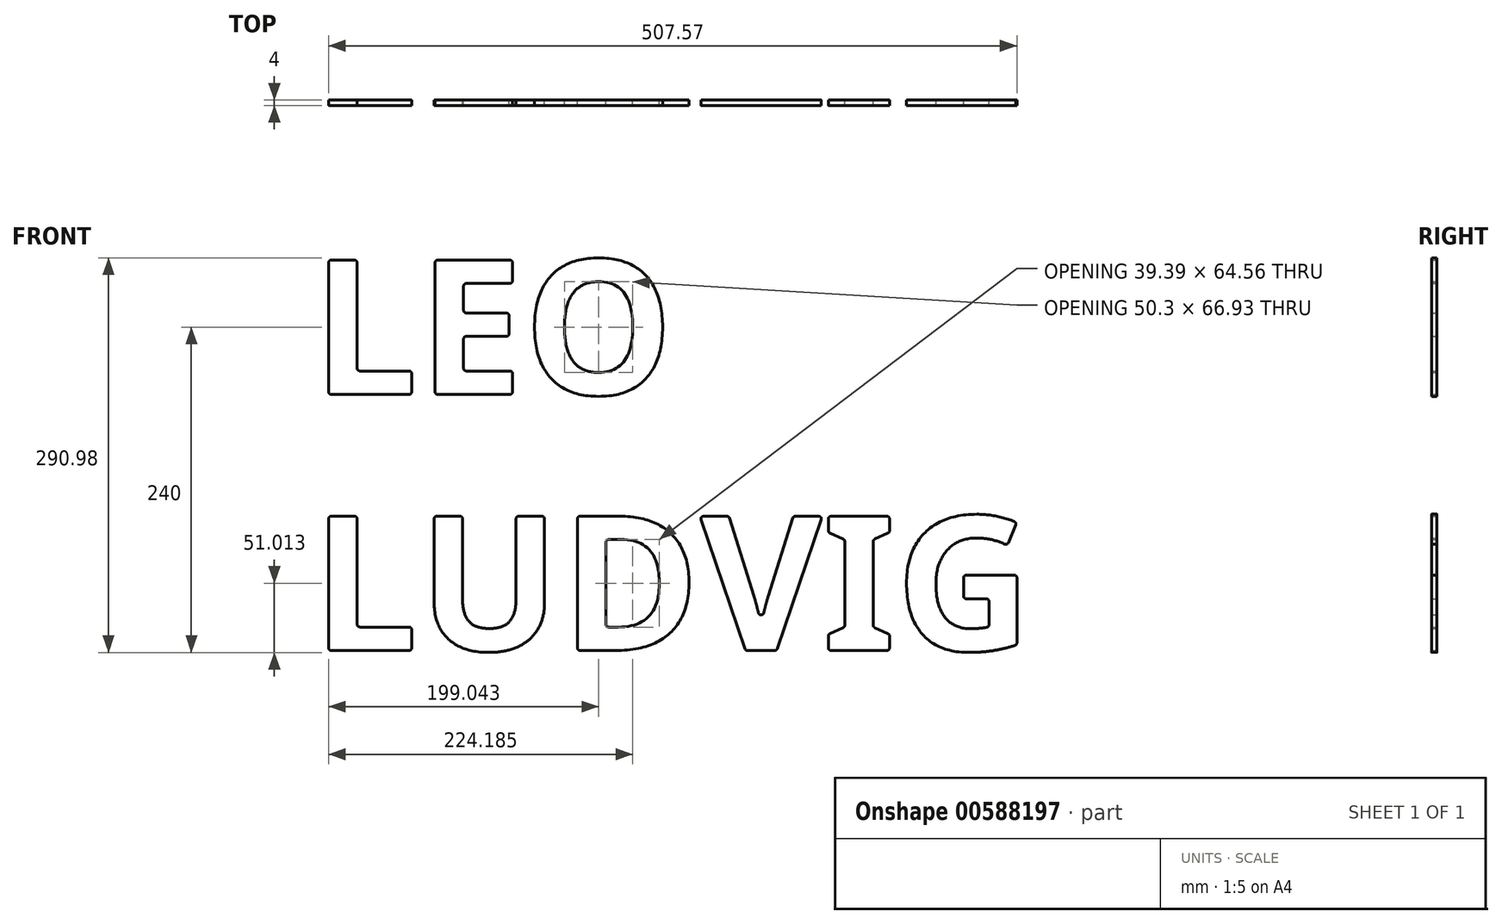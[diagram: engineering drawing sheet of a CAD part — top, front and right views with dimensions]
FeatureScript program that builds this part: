
annotation { "Feature Type Name" : "Feature", "Feature Type Description" : "" }
export const myFeature = defineFeature(function(context is Context, id is Id, definition is map)
    precondition{}
    {
        {
            var Q0;
            Q0=qCreatedBy(makeId("Front.planeOp"),FACE);
            var sketch = newSketch(context, id + "F0", { "sketchPlane" : qUnion([Q0])});
            skText(sketch, "E0", { "text": "LEO\nLUDVIG\n", "fontName": "NotoSans-Bold.ttf"});
            const initialGuessF0  = {"E0": [-0.26453, 0, 1, 0, 0.1]};
            skSetInitialGuess(sketch, initialGuessF0);
            skSolve(sketch);
        }
        {
            var Q0;
            Q0 = qSketchRegion(id + "F0", true);
            extrude(context, id + "F1", {"entities" : qUnion([Q0]), "depth" : 4 * mm, "offsetDistance" : 25 * mm});
        }
        {
            var Q0;
            Q0=makeQuery(id+"F1.opExtrude","SWEPT_EDGE",EDGE,{"disambiguationData":[OSD([sQuery(id+"F0.wireOp",EDGE,"E0.sketch_text.stroke-0"),sQuery(id+"F0.wireOp",EDGE,"E0.sketch_text.stroke-1")])]});
            var Q1;
            Q1=makeQuery(id+"F1.opExtrude","SWEPT_EDGE",EDGE,{"disambiguationData":[OSD([sQuery(id+"F0.wireOp",EDGE,"E0.sketch_text.stroke-1"),sQuery(id+"F0.wireOp",EDGE,"E0.sketch_text.stroke-2")])]});
            var Q2;
            Q2=makeQuery(id+"F1.opExtrude","SWEPT_EDGE",EDGE,{"disambiguationData":[OSD([sQuery(id+"F0.wireOp",EDGE,"E0.sketch_text.stroke-0"),sQuery(id+"F0.wireOp",EDGE,"E0.sketch_text.stroke-5")])]});
            var Q3;
            Q3=makeQuery(id+"F1.opExtrude","SWEPT_EDGE",EDGE,{"disambiguationData":[OSD([sQuery(id+"F0.wireOp",EDGE,"E0.sketch_text.stroke-3"),sQuery(id+"F0.wireOp",EDGE,"E0.sketch_text.stroke-4")])]});
            var Q4;
            Q4=makeQuery(id+"F1.opExtrude","SWEPT_EDGE",EDGE,{"disambiguationData":[OSD([sQuery(id+"F0.wireOp",EDGE,"E0.sketch_text.stroke-2"),sQuery(id+"F0.wireOp",EDGE,"E0.sketch_text.stroke-3")])]});
            var Q5;
            Q5=makeQuery(id+"F1.opExtrude","SWEPT_EDGE",EDGE,{"disambiguationData":[OSD([sQuery(id+"F0.wireOp",EDGE,"E0.sketch_text.stroke-4"),sQuery(id+"F0.wireOp",EDGE,"E0.sketch_text.stroke-5")])]});
            var Q6;
            Q6=makeQuery(id+"F1.opExtrude","SWEPT_EDGE",EDGE,{"disambiguationData":[OSD([sQuery(id+"F0.wireOp",EDGE,"E0.sketch_text.stroke-15"),sQuery(id+"F0.wireOp",EDGE,"E0.sketch_text.stroke-16")])]});
            var Q7;
            Q7=makeQuery(id+"F1.opExtrude","SWEPT_EDGE",EDGE,{"disambiguationData":[OSD([sQuery(id+"F0.wireOp",EDGE,"E0.sketch_text.stroke-16"),sQuery(id+"F0.wireOp",EDGE,"E0.sketch_text.stroke-17")])]});
            var Q8;
            Q8=makeQuery(id+"F1.opExtrude","SWEPT_EDGE",EDGE,{"disambiguationData":[OSD([sQuery(id+"F0.wireOp",EDGE,"E0.sketch_text.stroke-6"),sQuery(id+"F0.wireOp",EDGE,"E0.sketch_text.stroke-17")])]});
            var Q9;
            Q9=makeQuery(id+"F1.opExtrude","SWEPT_EDGE",EDGE,{"disambiguationData":[OSD([sQuery(id+"F0.wireOp",EDGE,"E0.sketch_text.stroke-13"),sQuery(id+"F0.wireOp",EDGE,"E0.sketch_text.stroke-14")])]});
            var Q10;
            Q10=makeQuery(id+"F1.opExtrude","SWEPT_EDGE",EDGE,{"disambiguationData":[OSD([sQuery(id+"F0.wireOp",EDGE,"E0.sketch_text.stroke-12"),sQuery(id+"F0.wireOp",EDGE,"E0.sketch_text.stroke-13")])]});
            var Q11;
            Q11=makeQuery(id+"F1.opExtrude","SWEPT_EDGE",EDGE,{"disambiguationData":[OSD([sQuery(id+"F0.wireOp",EDGE,"E0.sketch_text.stroke-11"),sQuery(id+"F0.wireOp",EDGE,"E0.sketch_text.stroke-12")])]});
            var Q12;
            Q12=makeQuery(id+"F1.opExtrude","SWEPT_EDGE",EDGE,{"disambiguationData":[OSD([sQuery(id+"F0.wireOp",EDGE,"E0.sketch_text.stroke-9"),sQuery(id+"F0.wireOp",EDGE,"E0.sketch_text.stroke-10")])]});
            var Q13;
            Q13=makeQuery(id+"F1.opExtrude","SWEPT_EDGE",EDGE,{"disambiguationData":[OSD([sQuery(id+"F0.wireOp",EDGE,"E0.sketch_text.stroke-8"),sQuery(id+"F0.wireOp",EDGE,"E0.sketch_text.stroke-9")])]});
            var Q14;
            Q14=makeQuery(id+"F1.opExtrude","SWEPT_EDGE",EDGE,{"disambiguationData":[OSD([sQuery(id+"F0.wireOp",EDGE,"E0.sketch_text.stroke-7"),sQuery(id+"F0.wireOp",EDGE,"E0.sketch_text.stroke-8")])]});
            var Q15;
            Q15=makeQuery(id+"F1.opExtrude","SWEPT_EDGE",EDGE,{"disambiguationData":[OSD([sQuery(id+"F0.wireOp",EDGE,"E0.sketch_text.stroke-6"),sQuery(id+"F0.wireOp",EDGE,"E0.sketch_text.stroke-7")])]});
            var Q16;
            Q16=makeQuery(id+"F1.opExtrude","SWEPT_EDGE",EDGE,{"disambiguationData":[OSD([sQuery(id+"F0.wireOp",EDGE,"E0.sketch_text.stroke-14"),sQuery(id+"F0.wireOp",EDGE,"E0.sketch_text.stroke-15")])]});
            var Q17;
            Q17=makeQuery(id+"F1.opExtrude","SWEPT_EDGE",EDGE,{"disambiguationData":[OSD([sQuery(id+"F0.wireOp",EDGE,"E0.sketch_text.stroke-10"),sQuery(id+"F0.wireOp",EDGE,"E0.sketch_text.stroke-11")])]});
            var Q18;
            Q18=makeQuery(id+"F1.opExtrude","SWEPT_EDGE",EDGE,{"disambiguationData":[OSD([sQuery(id+"F0.wireOp",EDGE,"E0.sketch_text.stroke-44"),sQuery(id+"F0.wireOp",EDGE,"E0.sketch_text.stroke-45")])]});
            var Q19;
            Q19=makeQuery(id+"F1.opExtrude","SWEPT_EDGE",EDGE,{"disambiguationData":[OSD([sQuery(id+"F0.wireOp",EDGE,"E0.sketch_text.stroke-45"),sQuery(id+"F0.wireOp",EDGE,"E0.sketch_text.stroke-46")])]});
            var Q20;
            Q20=makeQuery(id+"F1.opExtrude","SWEPT_EDGE",EDGE,{"disambiguationData":[OSD([sQuery(id+"F0.wireOp",EDGE,"E0.sketch_text.stroke-51"),sQuery(id+"F0.wireOp",EDGE,"E0.sketch_text.stroke-52")])]});
            var Q21;
            Q21=makeQuery(id+"F1.opExtrude","SWEPT_EDGE",EDGE,{"disambiguationData":[OSD([sQuery(id+"F0.wireOp",EDGE,"E0.sketch_text.stroke-38"),sQuery(id+"F0.wireOp",EDGE,"E0.sketch_text.stroke-52")])]});
            var Q22;
            Q22=makeQuery(id+"F1.opExtrude","SWEPT_EDGE",EDGE,{"disambiguationData":[OSD([sQuery(id+"F0.wireOp",EDGE,"E0.sketch_text.stroke-56"),sQuery(id+"F0.wireOp",EDGE,"E0.sketch_text.stroke-57")])]});
            var Q23;
            Q23=makeQuery(id+"F1.opExtrude","SWEPT_EDGE",EDGE,{"disambiguationData":[OSD([sQuery(id+"F0.wireOp",EDGE,"E0.sketch_text.stroke-62"),sQuery(id+"F0.wireOp",EDGE,"E0.sketch_text.stroke-63")])]});
            var Q24;
            Q24=makeQuery(id+"F1.opExtrude","SWEPT_EDGE",EDGE,{"disambiguationData":[OSD([sQuery(id+"F0.wireOp",EDGE,"E0.sketch_text.stroke-61"),sQuery(id+"F0.wireOp",EDGE,"E0.sketch_text.stroke-62")])]});
            var Q25;
            Q25=makeQuery(id+"F1.opExtrude","SWEPT_EDGE",EDGE,{"disambiguationData":[OSD([sQuery(id+"F0.wireOp",EDGE,"E0.sketch_text.stroke-55"),sQuery(id+"F0.wireOp",EDGE,"E0.sketch_text.stroke-56")])]});
            var Q26;
            Q26=makeQuery(id+"F1.opExtrude","SWEPT_EDGE",EDGE,{"disambiguationData":[OSD([sQuery(id+"F0.wireOp",EDGE,"E0.sketch_text.stroke-67"),sQuery(id+"F0.wireOp",EDGE,"E0.sketch_text.stroke-68")])]});
            var Q27;
            Q27=makeQuery(id+"F1.opExtrude","SWEPT_EDGE",EDGE,{"disambiguationData":[OSD([sQuery(id+"F0.wireOp",EDGE,"E0.sketch_text.stroke-66"),sQuery(id+"F0.wireOp",EDGE,"E0.sketch_text.stroke-67")])]});
            var Q28;
            Q28=makeQuery(id+"F1.opExtrude","SWEPT_EDGE",EDGE,{"disambiguationData":[OSD([sQuery(id+"F0.wireOp",EDGE,"E0.sketch_text.stroke-72"),sQuery(id+"F0.wireOp",EDGE,"E0.sketch_text.stroke-73")])]});
            var Q29;
            Q29=makeQuery(id+"F1.opExtrude","SWEPT_EDGE",EDGE,{"disambiguationData":[OSD([sQuery(id+"F0.wireOp",EDGE,"E0.sketch_text.stroke-73"),sQuery(id+"F0.wireOp",EDGE,"E0.sketch_text.stroke-74")])]});
            var Q30;
            Q30=makeQuery(id+"F1.opExtrude","SWEPT_EDGE",EDGE,{"disambiguationData":[OSD([sQuery(id+"F0.wireOp",EDGE,"E0.sketch_text.stroke-70"),sQuery(id+"F0.wireOp",EDGE,"E0.sketch_text.stroke-71")])]});
            var Q31;
            Q31=makeQuery(id+"F1.opExtrude","SWEPT_EDGE",EDGE,{"disambiguationData":[OSD([sQuery(id+"F0.wireOp",EDGE,"E0.sketch_text.stroke-68"),sQuery(id+"F0.wireOp",EDGE,"E0.sketch_text.stroke-69")])]});
            var Q32;
            Q32=makeQuery(id+"F1.opExtrude","SWEPT_EDGE",EDGE,{"disambiguationData":[OSD([sQuery(id+"F0.wireOp",EDGE,"E0.sketch_text.stroke-69"),sQuery(id+"F0.wireOp",EDGE,"E0.sketch_text.stroke-70")])]});
            var Q33;
            Q33=makeQuery(id+"F1.opExtrude","SWEPT_EDGE",EDGE,{"disambiguationData":[OSD([sQuery(id+"F0.wireOp",EDGE,"E0.sketch_text.stroke-65"),sQuery(id+"F0.wireOp",EDGE,"E0.sketch_text.stroke-74")])]});
            var Q34;
            Q34=makeQuery(id+"F1.opExtrude","SWEPT_EDGE",EDGE,{"disambiguationData":[OSD([sQuery(id+"F0.wireOp",EDGE,"E0.sketch_text.stroke-65"),sQuery(id+"F0.wireOp",EDGE,"E0.sketch_text.stroke-66")])]});
            var Q35;
            Q35=makeQuery(id+"F1.opExtrude","SWEPT_EDGE",EDGE,{"disambiguationData":[OSD([sQuery(id+"F0.wireOp",EDGE,"E0.sketch_text.stroke-80"),sQuery(id+"F0.wireOp",EDGE,"E0.sketch_text.stroke-81")])]});
            var Q36;
            Q36=makeQuery(id+"F1.opExtrude","SWEPT_EDGE",EDGE,{"disambiguationData":[OSD([sQuery(id+"F0.wireOp",EDGE,"E0.sketch_text.stroke-81"),sQuery(id+"F0.wireOp",EDGE,"E0.sketch_text.stroke-82")])]});
            var Q37;
            Q37=makeQuery(id+"F1.opExtrude","SWEPT_EDGE",EDGE,{"disambiguationData":[OSD([sQuery(id+"F0.wireOp",EDGE,"E0.sketch_text.stroke-79"),sQuery(id+"F0.wireOp",EDGE,"E0.sketch_text.stroke-80")])]});
            var Q38;
            Q38=makeQuery(id+"F1.opExtrude","SWEPT_EDGE",EDGE,{"disambiguationData":[OSD([sQuery(id+"F0.wireOp",EDGE,"E0.sketch_text.stroke-78"),sQuery(id+"F0.wireOp",EDGE,"E0.sketch_text.stroke-79")])]});
            var Q39;
            Q39=makeQuery(id+"F1.opExtrude","SWEPT_EDGE",EDGE,{"disambiguationData":[OSD([sQuery(id+"F0.wireOp",EDGE,"E0.sketch_text.stroke-75"),sQuery(id+"F0.wireOp",EDGE,"E0.sketch_text.stroke-76")])]});
            var Q40;
            Q40=makeQuery(id+"F1.opExtrude","SWEPT_EDGE",EDGE,{"disambiguationData":[OSD([sQuery(id+"F0.wireOp",EDGE,"E0.sketch_text.stroke-76"),sQuery(id+"F0.wireOp",EDGE,"E0.sketch_text.stroke-77")])]});
            var Q41;
            Q41=makeQuery(id+"F1.opExtrude","SWEPT_EDGE",EDGE,{"disambiguationData":[OSD([sQuery(id+"F0.wireOp",EDGE,"E0.sketch_text.stroke-77"),sQuery(id+"F0.wireOp",EDGE,"E0.sketch_text.stroke-78")])]});
            var Q42;
            Q42=makeQuery(id+"F1.opExtrude","SWEPT_EDGE",EDGE,{"disambiguationData":[OSD([sQuery(id+"F0.wireOp",EDGE,"E0.sketch_text.stroke-75"),sQuery(id+"F0.wireOp",EDGE,"E0.sketch_text.stroke-86")])]});
            var Q43;
            Q43=makeQuery(id+"F1.opExtrude","SWEPT_EDGE",EDGE,{"disambiguationData":[OSD([sQuery(id+"F0.wireOp",EDGE,"E0.sketch_text.stroke-84"),sQuery(id+"F0.wireOp",EDGE,"E0.sketch_text.stroke-85")])]});
            var Q44;
            Q44=makeQuery(id+"F1.opExtrude","SWEPT_EDGE",EDGE,{"disambiguationData":[OSD([sQuery(id+"F0.wireOp",EDGE,"E0.sketch_text.stroke-85"),sQuery(id+"F0.wireOp",EDGE,"E0.sketch_text.stroke-86")])]});
            var Q45;
            Q45=makeQuery(id+"F1.opExtrude","SWEPT_EDGE",EDGE,{"disambiguationData":[OSD([sQuery(id+"F0.wireOp",EDGE,"E0.sketch_text.stroke-82"),sQuery(id+"F0.wireOp",EDGE,"E0.sketch_text.stroke-83")])]});
            var Q46;
            Q46=makeQuery(id+"F1.opExtrude","SWEPT_EDGE",EDGE,{"disambiguationData":[OSD([sQuery(id+"F0.wireOp",EDGE,"E0.sketch_text.stroke-83"),sQuery(id+"F0.wireOp",EDGE,"E0.sketch_text.stroke-84")])]});
            var Q47;
            Q47=makeQuery(id+"F1.opExtrude","SWEPT_EDGE",EDGE,{"disambiguationData":[OSD([sQuery(id+"F0.wireOp",EDGE,"E0.sketch_text.stroke-95"),sQuery(id+"F0.wireOp",EDGE,"E0.sketch_text.stroke-96")])]});
            var Q48;
            Q48=makeQuery(id+"F1.opExtrude","SWEPT_EDGE",EDGE,{"disambiguationData":[OSD([sQuery(id+"F0.wireOp",EDGE,"E0.sketch_text.stroke-96"),sQuery(id+"F0.wireOp",EDGE,"E0.sketch_text.stroke-97")])]});
            var Q49;
            Q49=makeQuery(id+"F1.opExtrude","SWEPT_EDGE",EDGE,{"disambiguationData":[OSD([sQuery(id+"F0.wireOp",EDGE,"E0.sketch_text.stroke-87"),sQuery(id+"F0.wireOp",EDGE,"E0.sketch_text.stroke-88")])]});
            var Q50;
            Q50=makeQuery(id+"F1.opExtrude","SWEPT_EDGE",EDGE,{"disambiguationData":[OSD([sQuery(id+"F0.wireOp",EDGE,"E0.sketch_text.stroke-102"),sQuery(id+"F0.wireOp",EDGE,"E0.sketch_text.stroke-103")])]});
            var Q51;
            Q51=makeQuery(id+"F1.opExtrude","SWEPT_EDGE",EDGE,{"disambiguationData":[OSD([sQuery(id+"F0.wireOp",EDGE,"E0.sketch_text.stroke-87"),sQuery(id+"F0.wireOp",EDGE,"E0.sketch_text.stroke-105")])]});
            var Q52;
            Q52=makeQuery(id+"F1.opExtrude","SWEPT_EDGE",EDGE,{"disambiguationData":[OSD([sQuery(id+"F0.wireOp",EDGE,"E0.sketch_text.stroke-104"),sQuery(id+"F0.wireOp",EDGE,"E0.sketch_text.stroke-105")])]});
            var Q53;
            Q53=makeQuery(id+"F1.opExtrude","SWEPT_EDGE",EDGE,{"disambiguationData":[OSD([sQuery(id+"F0.wireOp",EDGE,"E0.sketch_text.stroke-103"),sQuery(id+"F0.wireOp",EDGE,"E0.sketch_text.stroke-104")])]});
            var Q54;
            Q54=makeQuery(id+"F1.opExtrude","SWEPT_EDGE",EDGE,{"disambiguationData":[OSD([sQuery(id+"F0.wireOp",EDGE,"E0.sketch_text.stroke-88"),sQuery(id+"F0.wireOp",EDGE,"E0.sketch_text.stroke-89")])]});
            var Q55;
            Q55=makeQuery(id+"F1.opExtrude","SWEPT_EDGE",EDGE,{"disambiguationData":[OSD([sQuery(id+"F0.wireOp",EDGE,"E0.sketch_text.stroke-32"),sQuery(id+"F0.wireOp",EDGE,"E0.sketch_text.stroke-33")])]});
            var Q56;
            Q56=makeQuery(id+"F1.opExtrude","SWEPT_EDGE",EDGE,{"disambiguationData":[OSD([sQuery(id+"F0.wireOp",EDGE,"E0.sketch_text.stroke-33"),sQuery(id+"F0.wireOp",EDGE,"E0.sketch_text.stroke-34")])]});
            var Q57;
            Q57=makeQuery(id+"F1.opExtrude","SWEPT_EDGE",EDGE,{"disambiguationData":[OSD([sQuery(id+"F0.wireOp",EDGE,"E0.sketch_text.stroke-35"),sQuery(id+"F0.wireOp",EDGE,"E0.sketch_text.stroke-36")])]});
            var Q58;
            Q58=makeQuery(id+"F1.opExtrude","SWEPT_EDGE",EDGE,{"disambiguationData":[OSD([sQuery(id+"F0.wireOp",EDGE,"E0.sketch_text.stroke-32"),sQuery(id+"F0.wireOp",EDGE,"E0.sketch_text.stroke-37")])]});
            var Q59;
            Q59=makeQuery(id+"F1.opExtrude","SWEPT_EDGE",EDGE,{"disambiguationData":[OSD([sQuery(id+"F0.wireOp",EDGE,"E0.sketch_text.stroke-34"),sQuery(id+"F0.wireOp",EDGE,"E0.sketch_text.stroke-35")])]});
            var Q60;
            Q60=makeQuery(id+"F1.opExtrude","SWEPT_EDGE",EDGE,{"disambiguationData":[OSD([sQuery(id+"F0.wireOp",EDGE,"E0.sketch_text.stroke-36"),sQuery(id+"F0.wireOp",EDGE,"E0.sketch_text.stroke-37")])]});
            fillet(context, id + "F2", {"entities" : qUnion([Q0, Q1, Q2, Q3, Q4, Q5, Q6, Q7, Q8, Q9, Q10, Q11, Q12, Q13, Q14, Q15, Q16, Q17, Q18, Q19, Q20, Q21, Q22, Q23, Q24, Q25, Q26, Q27, Q28, Q29, Q30, Q31, Q32, Q33, Q34, Q35, Q36, Q37, Q38, Q39, Q40, Q41, Q42, Q43, Q44, Q45, Q46, Q47, Q48, Q49, Q50, Q51, Q52, Q53, Q54, Q55, Q56, Q57, Q58, Q59, Q60]), "radius" : 2 * mm, "tangentPropagation" : true, "allowEdgeOverflow" : false});
        }
    });
